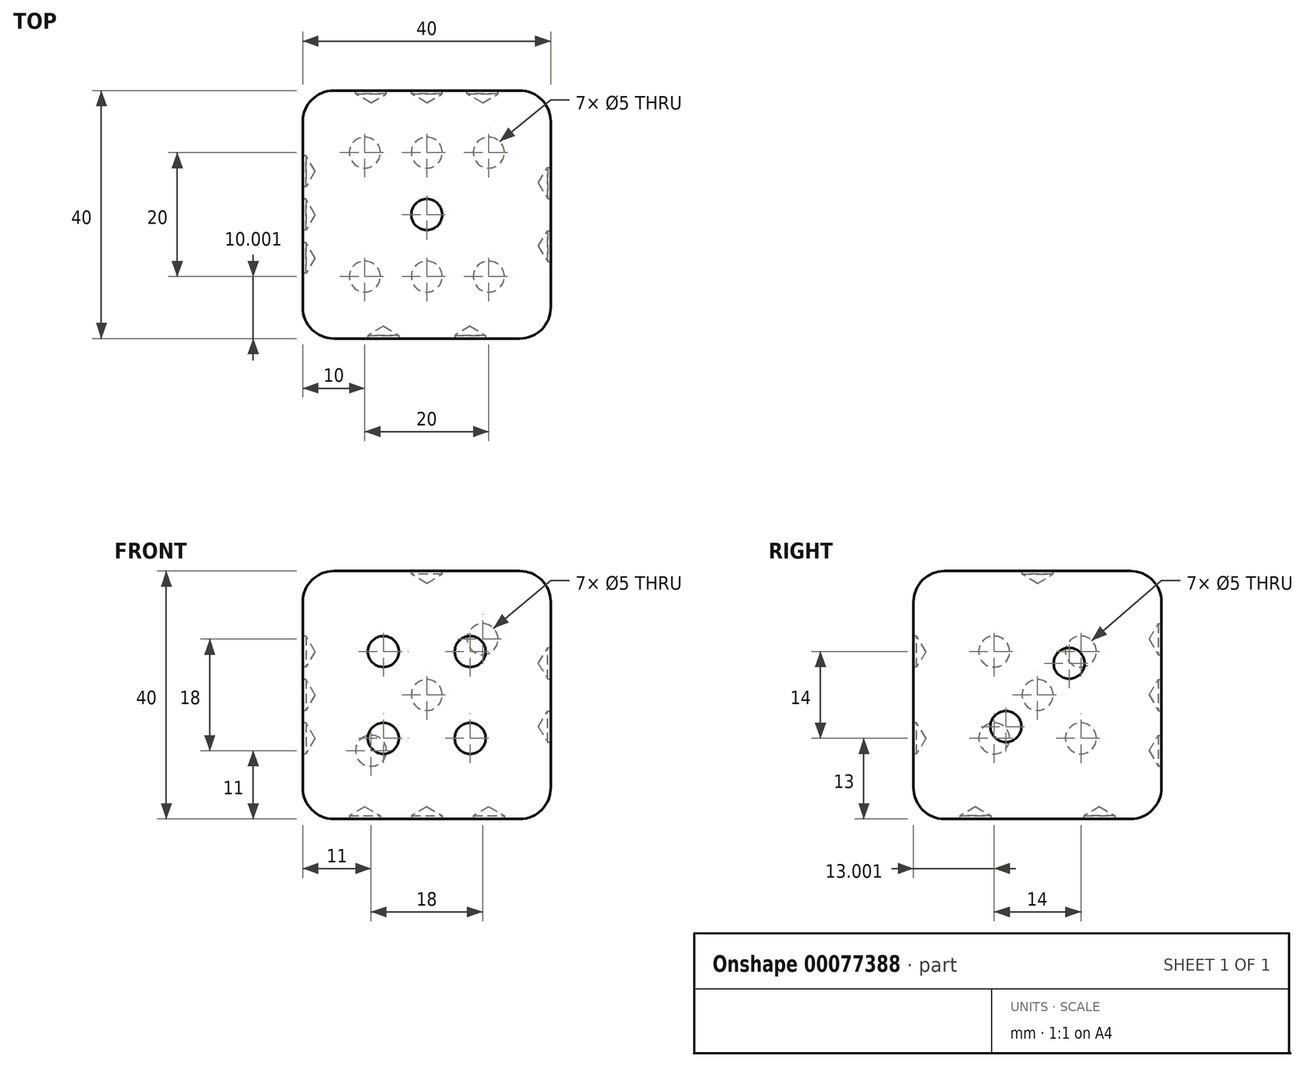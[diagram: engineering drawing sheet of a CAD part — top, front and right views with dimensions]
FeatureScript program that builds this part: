
annotation { "Feature Type Name" : "Feature", "Feature Type Description" : "" }
export const myFeature = defineFeature(function(context is Context, id is Id, definition is map)
    precondition{}
    {
        {
            var Q0;
            Q0=qCreatedBy(makeId("Top.planeOp"),FACE);
            var sketch = newSketch(context, id + "F0", { "sketchPlane" : qUnion([Q0])});
            skLineSegment(sketch, "E0.bottom", {"start": v(0, -2.27) * mm, "end": v(40, -2.27) * mm});
            skLineSegment(sketch, "E0.top", {"start": v(0, 37.73) * mm, "end": v(40, 37.73) * mm});
            skLineSegment(sketch, "E0.left", {"start": v(0, -2.27) * mm, "end": v(0, 37.73) * mm});
            skLineSegment(sketch, "E0.right", {"start": v(40, -2.27) * mm, "end": v(40, 37.73) * mm});
            skSolve(sketch);
        }
        {
            var Q0;
            Q0=makeQuery(id+"F0.imprint","IMPRINT",FACE,{"disambiguationData":[TD([[makeQuery(id+"F0.imprint","IMPRINT",EDGE,{"derivedFrom":sQuery(id+"F0.wireOp",EDGE,"E0.bottom")}),1.0]])]});
            extrude(context, id + "F1", {"entities" : qUnion([Q0]), "depth" : 40 * mm});
        }
        {
            var Q0;
            Q0=makeQuery(id+"F1.opExtrude","CAP_EDGE",EDGE,{"disambiguationData":[OSD([sQuery(id+"F0.wireOp",EDGE,"E0.left")])],"isStart":false});
            var Q1;
            Q1=makeQuery(id+"F1.opExtrude","CAP_EDGE",EDGE,{"disambiguationData":[OSD([sQuery(id+"F0.wireOp",EDGE,"E0.bottom")])],"isStart":false});
            var Q2;
            Q2=makeQuery(id+"F1.opExtrude","CAP_EDGE",EDGE,{"disambiguationData":[OSD([sQuery(id+"F0.wireOp",EDGE,"E0.right")])],"isStart":false});
            var Q3;
            Q3=makeQuery(id+"F1.opExtrude","CAP_EDGE",EDGE,{"disambiguationData":[OSD([sQuery(id+"F0.wireOp",EDGE,"E0.top")])],"isStart":false});
            var Q4;
            Q4=makeQuery(id+"F1.opExtrude","SWEPT_EDGE",EDGE,{"disambiguationData":[OSD([sQuery(id+"F0.wireOp",EDGE,"E0.bottom"),sQuery(id+"F0.wireOp",EDGE,"E0.left")])]});
            var Q5;
            Q5=makeQuery(id+"F1.opExtrude","SWEPT_EDGE",EDGE,{"disambiguationData":[OSD([sQuery(id+"F0.wireOp",EDGE,"E0.bottom"),sQuery(id+"F0.wireOp",EDGE,"E0.right")])]});
            var Q6;
            Q6=makeQuery(id+"F1.opExtrude","SWEPT_EDGE",EDGE,{"disambiguationData":[OSD([sQuery(id+"F0.wireOp",EDGE,"E0.top"),sQuery(id+"F0.wireOp",EDGE,"E0.left")])]});
            var Q7;
            Q7=makeQuery(id+"F1.opExtrude","CAP_EDGE",EDGE,{"disambiguationData":[OSD([sQuery(id+"F0.wireOp",EDGE,"E0.bottom")])],"isStart":true});
            var Q8;
            Q8=makeQuery(id+"F1.opExtrude","CAP_EDGE",EDGE,{"disambiguationData":[OSD([sQuery(id+"F0.wireOp",EDGE,"E0.left")])],"isStart":true});
            var Q9;
            Q9=makeQuery(id+"F1.opExtrude","CAP_EDGE",EDGE,{"disambiguationData":[OSD([sQuery(id+"F0.wireOp",EDGE,"E0.right")])],"isStart":true});
            var Q10;
            Q10=makeQuery(id+"F1.opExtrude","CAP_EDGE",EDGE,{"disambiguationData":[OSD([sQuery(id+"F0.wireOp",EDGE,"E0.top")])],"isStart":true});
            var Q11;
            Q11=makeQuery(id+"F1.opExtrude","SWEPT_EDGE",EDGE,{"disambiguationData":[OSD([sQuery(id+"F0.wireOp",EDGE,"E0.top"),sQuery(id+"F0.wireOp",EDGE,"E0.right")])]});
            fillet(context, id + "F2", {"entities" : qUnion([Q0, Q1, Q2, Q3, Q4, Q5, Q6, Q7, Q8, Q9, Q10, Q11]), "radius" : 5 * mm, "tangentPropagation" : true, "allowEdgeOverflow" : false});
        }
        {
            var Q0;
            Q0=makeQuery(id+"F1.opExtrude","CAP_FACE",FACE,{"disambiguationData":[OSD([sQuery(id+"F0.wireOp",EDGE,"E0.bottom"),sQuery(id+"F0.wireOp",EDGE,"E0.top"),sQuery(id+"F0.wireOp",EDGE,"E0.left"),sQuery(id+"F0.wireOp",EDGE,"E0.right")])],"isStart":false});
            var sketch = newSketch(context, id + "F3", { "sketchPlane" : qUnion([Q0])});
            skLineSegment(sketch, "E1", {"start": v(5, 32.73) * mm, "end": v(35, 2.73) * mm});
            skLineSegment(sketch, "E2", {"start": v(35, 32.73) * mm, "end": v(5, 2.73) * mm});
            skPoint(sketch, "E3", {"position": v(20, 17.73) * mm});
            skSolve(sketch);
        }
        {
            var Q0;
            Q0=sQuery(id+"F3.wireOp",VERTEX,"E3");
            var Q1;
            Q1=makeQuery(id+"F1.opExtrude","SWEPT_BODY",BODY,{"disambiguationData":[OSD([sQuery(id+"F0.wireOp",EDGE,"E0.bottom"),sQuery(id+"F0.wireOp",EDGE,"E0.top"),sQuery(id+"F0.wireOp",EDGE,"E0.left"),sQuery(id+"F0.wireOp",EDGE,"E0.right")])]});
            hole(context, id + "F4", {"style" : HoleStyle.SIMPLE, "endStyle" : HoleEndStyle.BLIND, "holeDiameter" : 5 * mm, "holeDepth" : 0.5 * mm, "locations" : qUnion([Q0]), "scope" : qUnion([Q1])});
        }
        {
            var Q0;
            Q0=makeQuery(id+"F1.opExtrude","CAP_FACE",FACE,{"disambiguationData":[OSD([sQuery(id+"F0.wireOp",EDGE,"E0.bottom"),sQuery(id+"F0.wireOp",EDGE,"E0.top"),sQuery(id+"F0.wireOp",EDGE,"E0.left"),sQuery(id+"F0.wireOp",EDGE,"E0.right")])],"isStart":true});
            var sketch = newSketch(context, id + "F5", { "sketchPlane" : qUnion([Q0])});
            skLineSegment(sketch, "E4", {"start": v(35, -32.73) * mm, "end": v(5, -2.73) * mm});
            skLineSegment(sketch, "E5", {"start": v(5, -32.73) * mm, "end": v(35, -2.73) * mm});
            skLineSegment(sketch, "E6", {"start": v(20, -32.73) * mm, "end": v(20, 0) * mm});
            skLineSegment(sketch, "E7", {"start": v(20, -33.86) * mm, "end": v(30, -33.86) * mm});
            skLineSegment(sketch, "E8", {"start": v(30, -32.73) * mm, "end": v(30, 0) * mm});
            skLineSegment(sketch, "E9", {"start": v(20, -33.86) * mm, "end": v(10, -33.86) * mm});
            skLineSegment(sketch, "E10", {"start": v(10, -32.73) * mm, "end": v(10, -2.73) * mm});
            skLineSegment(sketch, "E11", {"start": v(30, -7.73) * mm, "end": v(10, -7.73) * mm});
            skLineSegment(sketch, "E12", {"start": v(30, -27.73) * mm, "end": v(10, -27.73) * mm});
            skPoint(sketch, "E13", {"position": v(30, -27.73) * mm});
            skPoint(sketch, "E14", {"position": v(20, -27.73) * mm});
            skPoint(sketch, "E15", {"position": v(10, -27.73) * mm});
            skPoint(sketch, "E16", {"position": v(10, -7.73) * mm});
            skPoint(sketch, "E17", {"position": v(20, -7.73) * mm});
            skPoint(sketch, "E18", {"position": v(30, -7.73) * mm});
            skSolve(sketch);
        }
        {
            var Q0;
            Q0=sQuery(id+"F5.wireOp",VERTEX,"E13");
            var Q1;
            Q1=sQuery(id+"F5.wireOp",VERTEX,"E14");
            var Q2;
            Q2=sQuery(id+"F5.wireOp",VERTEX,"E15");
            var Q3;
            Q3=sQuery(id+"F5.wireOp",VERTEX,"E16");
            var Q4;
            Q4=sQuery(id+"F5.wireOp",VERTEX,"E17");
            var Q5;
            Q5=sQuery(id+"F5.wireOp",VERTEX,"E18");
            var Q6;
            Q6=makeQuery(id+"F1.opExtrude","SWEPT_BODY",BODY,{"disambiguationData":[OSD([sQuery(id+"F0.wireOp",EDGE,"E0.bottom"),sQuery(id+"F0.wireOp",EDGE,"E0.top"),sQuery(id+"F0.wireOp",EDGE,"E0.left"),sQuery(id+"F0.wireOp",EDGE,"E0.right")])]});
            hole(context, id + "F6", {"style" : HoleStyle.SIMPLE, "endStyle" : HoleEndStyle.BLIND, "holeDiameter" : 5 * mm, "holeDepth" : 0.5 * mm, "locations" : qUnion([Q0, Q1, Q2, Q3, Q4, Q5]), "scope" : qUnion([Q6])});
        }
        {
            var Q0;
            Q0=makeQuery(id+"F1.opExtrude","SWEPT_FACE",FACE,{"disambiguationData":[OSD([sQuery(id+"F0.wireOp",EDGE,"E0.top")])]});
            var sketch = newSketch(context, id + "F7", { "sketchPlane" : qUnion([Q0])});
            skLineSegment(sketch, "E19", {"start": v(-35, 5) * mm, "end": v(-5, 35) * mm});
            skLineSegment(sketch, "E20", {"start": v(-35, 35) * mm, "end": v(-5, 5) * mm});
            skPoint(sketch, "E21", {"position": v(-20, 20) * mm});
            skLineSegment(sketch, "E22", {"start": v(-5, 5) * mm, "end": v(-11, 11) * mm});
            skLineSegment(sketch, "E23", {"start": v(-35, 35) * mm, "end": v(-29, 29) * mm});
            skPoint(sketch, "E24", {"position": v(-29, 29) * mm});
            skPoint(sketch, "E25", {"position": v(-11, 11) * mm});
            skSolve(sketch);
        }
        {
            var Q0;
            Q0=sQuery(id+"F7.wireOp",VERTEX,"E25");
            var Q1;
            Q1=sQuery(id+"F7.wireOp",VERTEX,"E21");
            var Q2;
            Q2=sQuery(id+"F7.wireOp",VERTEX,"E24");
            var Q3;
            Q3=makeQuery(id+"F1.opExtrude","SWEPT_BODY",BODY,{"disambiguationData":[OSD([sQuery(id+"F0.wireOp",EDGE,"E0.bottom"),sQuery(id+"F0.wireOp",EDGE,"E0.top"),sQuery(id+"F0.wireOp",EDGE,"E0.left"),sQuery(id+"F0.wireOp",EDGE,"E0.right")])]});
            hole(context, id + "F8", {"style" : HoleStyle.SIMPLE, "endStyle" : HoleEndStyle.BLIND, "holeDiameter" : 5 * mm, "holeDepth" : 0.5 * mm, "locations" : qUnion([Q0, Q1, Q2]), "scope" : qUnion([Q3])});
        }
        {
            var Q0;
            Q0=makeQuery(id+"F1.opExtrude","SWEPT_FACE",FACE,{"disambiguationData":[OSD([sQuery(id+"F0.wireOp",EDGE,"E0.bottom")])]});
            var sketch = newSketch(context, id + "F9", { "sketchPlane" : qUnion([Q0])});
            skLineSegment(sketch, "E26", {"start": v(5, 35) * mm, "end": v(35, 5) * mm});
            skLineSegment(sketch, "E27", {"start": v(35, 35) * mm, "end": v(5, 5) * mm});
            skLineSegment(sketch, "E28", {"start": v(5, 20) * mm, "end": v(13, 20) * mm});
            skPoint(sketch, "E28.startSnap0", {"position": v(5, 20) * mm});
            skLineSegment(sketch, "E29", {"start": v(13, 27) * mm, "end": v(27, 27) * mm});
            skLineSegment(sketch, "E30", {"start": v(27, 27) * mm, "end": v(27, 13) * mm});
            skLineSegment(sketch, "E31", {"start": v(27, 13) * mm, "end": v(13, 13) * mm});
            skLineSegment(sketch, "E32", {"start": v(13, 13) * mm, "end": v(13, 27) * mm});
            skPoint(sketch, "E33", {"position": v(13, 27) * mm});
            skPoint(sketch, "E34", {"position": v(27, 27) * mm});
            skPoint(sketch, "E35", {"position": v(27, 13) * mm});
            skPoint(sketch, "E36", {"position": v(13, 13) * mm});
            skSolve(sketch);
        }
        {
            var Q0;
            Q0=sQuery(id+"F9.wireOp",VERTEX,"E33");
            var Q1;
            Q1=sQuery(id+"F9.wireOp",VERTEX,"E34");
            var Q2;
            Q2=sQuery(id+"F9.wireOp",VERTEX,"E35");
            var Q3;
            Q3=sQuery(id+"F9.wireOp",VERTEX,"E36");
            var Q4;
            Q4=makeQuery(id+"F1.opExtrude","SWEPT_BODY",BODY,{"disambiguationData":[OSD([sQuery(id+"F0.wireOp",EDGE,"E0.bottom"),sQuery(id+"F0.wireOp",EDGE,"E0.top"),sQuery(id+"F0.wireOp",EDGE,"E0.left"),sQuery(id+"F0.wireOp",EDGE,"E0.right")])]});
            hole(context, id + "F10", {"style" : HoleStyle.SIMPLE, "endStyle" : HoleEndStyle.BLIND, "holeDiameter" : 5 * mm, "holeDepth" : 0.5 * mm, "locations" : qUnion([Q0, Q1, Q2, Q3]), "scope" : qUnion([Q4])});
        }
        {
            var Q0;
            Q0=makeQuery(id+"F1.opExtrude","SWEPT_FACE",FACE,{"disambiguationData":[OSD([sQuery(id+"F0.wireOp",EDGE,"E0.left")])]});
            var sketch = newSketch(context, id + "F11", { "sketchPlane" : qUnion([Q0])});
            skLineSegment(sketch, "E37", {"start": v(-32.73, 35) * mm, "end": v(-2.73, 5) * mm});
            skLineSegment(sketch, "E38", {"start": v(-2.73, 35) * mm, "end": v(-32.73, 5) * mm});
            skLineSegment(sketch, "E39", {"start": v(-32.73, 21.88) * mm, "end": v(-24.73, 21.88) * mm});
            skLineSegment(sketch, "E40", {"start": v(-24.73, 13) * mm, "end": v(-10.73, 13) * mm});
            skLineSegment(sketch, "E41", {"start": v(-10.73, 13) * mm, "end": v(-10.73, 27) * mm});
            skLineSegment(sketch, "E42", {"start": v(-10.73, 27) * mm, "end": v(-24.73, 27) * mm});
            skLineSegment(sketch, "E43", {"start": v(-24.73, 27) * mm, "end": v(-24.73, 13) * mm});
            skPoint(sketch, "E44", {"position": v(-24.73, 27) * mm});
            skPoint(sketch, "E45", {"position": v(-10.73, 27) * mm});
            skPoint(sketch, "E46", {"position": v(-10.73, 13) * mm});
            skPoint(sketch, "E47", {"position": v(-24.73, 13) * mm});
            skPoint(sketch, "E48", {"position": v(-17.73, 20) * mm});
            skSolve(sketch);
        }
        {
            var Q0;
            Q0=sQuery(id+"F11.wireOp",VERTEX,"E44");
            var Q1;
            Q1=sQuery(id+"F11.wireOp",VERTEX,"E45");
            var Q2;
            Q2=sQuery(id+"F11.wireOp",VERTEX,"E46");
            var Q3;
            Q3=sQuery(id+"F11.wireOp",VERTEX,"E47");
            var Q4;
            Q4=sQuery(id+"F11.wireOp",VERTEX,"E48");
            var Q5;
            Q5=makeQuery(id+"F1.opExtrude","SWEPT_BODY",BODY,{"disambiguationData":[OSD([sQuery(id+"F0.wireOp",EDGE,"E0.bottom"),sQuery(id+"F0.wireOp",EDGE,"E0.top"),sQuery(id+"F0.wireOp",EDGE,"E0.left"),sQuery(id+"F0.wireOp",EDGE,"E0.right")])]});
            hole(context, id + "F12", {"style" : HoleStyle.SIMPLE, "endStyle" : HoleEndStyle.BLIND, "holeDiameter" : 5 * mm, "holeDepth" : 0.5 * mm, "locations" : qUnion([Q0, Q1, Q2, Q3, Q4]), "scope" : qUnion([Q5])});
        }
        {
            var Q0;
            Q0=makeQuery(id+"F1.opExtrude","SWEPT_FACE",FACE,{"disambiguationData":[OSD([sQuery(id+"F0.wireOp",EDGE,"E0.right")])]});
            var sketch = newSketch(context, id + "F13", { "sketchPlane" : qUnion([Q0])});
            skLineSegment(sketch, "E49", {"start": v(32.73, 35) * mm, "end": v(22.83, 25.1) * mm});
            skLineSegment(sketch, "E50", {"start": v(2.73, 5) * mm, "end": v(12.63, 14.9) * mm});
            skPoint(sketch, "E51", {"position": v(12.63, 14.9) * mm});
            skPoint(sketch, "E52", {"position": v(22.83, 25.1) * mm});
            skSolve(sketch);
        }
        {
            var Q0;
            Q0=sQuery(id+"F13.wireOp",VERTEX,"E52");
            var Q1;
            Q1=sQuery(id+"F13.wireOp",VERTEX,"E51");
            var Q2;
            Q2=makeQuery(id+"F1.opExtrude","SWEPT_BODY",BODY,{"disambiguationData":[OSD([sQuery(id+"F0.wireOp",EDGE,"E0.bottom"),sQuery(id+"F0.wireOp",EDGE,"E0.top"),sQuery(id+"F0.wireOp",EDGE,"E0.left"),sQuery(id+"F0.wireOp",EDGE,"E0.right")])]});
            hole(context, id + "F14", {"style" : HoleStyle.SIMPLE, "endStyle" : HoleEndStyle.BLIND, "holeDiameter" : 5 * mm, "holeDepth" : 0.5 * mm, "locations" : qUnion([Q0, Q1]), "scope" : qUnion([Q2])});
        }
    });
